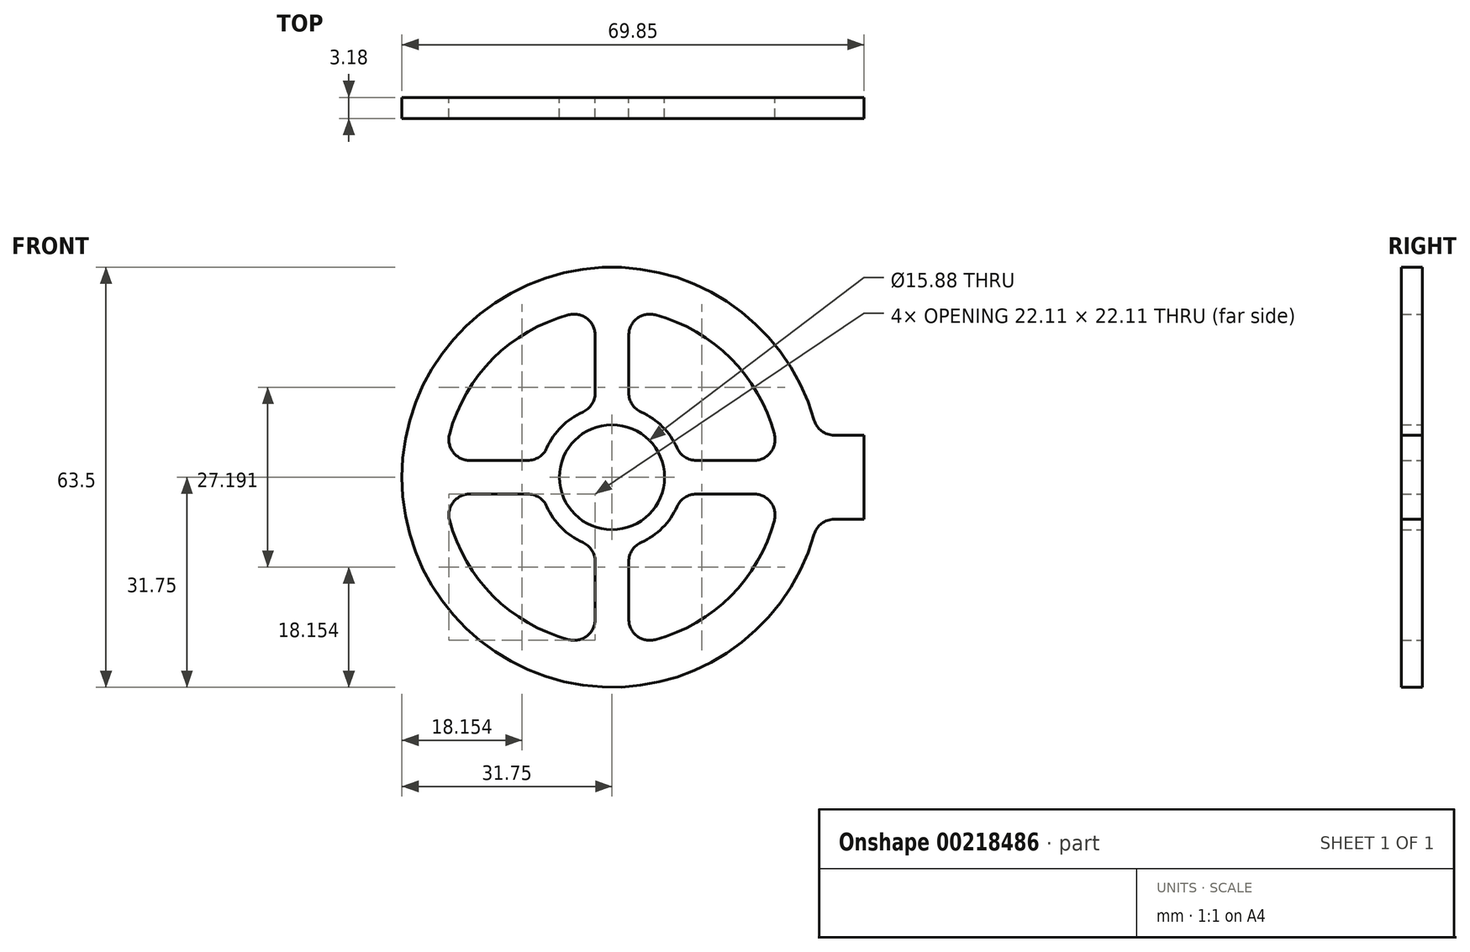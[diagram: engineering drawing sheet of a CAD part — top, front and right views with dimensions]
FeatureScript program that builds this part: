
annotation { "Feature Type Name" : "Feature", "Feature Type Description" : "" }
export const myFeature = defineFeature(function(context is Context, id is Id, definition is map)
    precondition{}
    {
        {
            var Q0;
            Q0=qCreatedBy(makeId("Front.planeOp"),FACE);
            var sketch = newSketch(context, id + "F0", { "sketchPlane" : qUnion([Q0])});
            skArc(sketch, "E0", {"start": v(30.55, 8.66) * mm, "mid": v(-31.75, 0) * mm, "end": v(30.55, -8.66) * mm});
            skLineSegment(sketch, "E1", {"start": v(-12.75, 2.54) * mm, "end": v(-21.48, 2.54) * mm});
            skLineSegment(sketch, "E2", {"start": v(-2.54, 12.75) * mm, "end": v(-2.54, 21.48) * mm});
            skLineSegment(sketch, "E3", {"start": v(2.54, 12.75) * mm, "end": v(2.54, 21.48) * mm});
            skLineSegment(sketch, "E4", {"start": v(12.75, 2.54) * mm, "end": v(21.48, 2.54) * mm});
            skLineSegment(sketch, "E5", {"start": v(-12.75, -2.54) * mm, "end": v(-21.48, -2.54) * mm});
            skLineSegment(sketch, "E6", {"start": v(12.75, -2.54) * mm, "end": v(21.48, -2.54) * mm});
            skLineSegment(sketch, "E7", {"start": v(-2.54, -12.75) * mm, "end": v(-2.54, -21.48) * mm});
            skLineSegment(sketch, "E8", {"start": v(2.54, -12.75) * mm, "end": v(2.54, -21.48) * mm});
            skArc(sketch, "E9", {"start": v(-6.53, 24.55) * mm, "mid": v(-17.96, 17.96) * mm, "end": v(-24.55, 6.53) * mm});
            skArc(sketch, "E10.trimOffspring", {"start": v(-24.55, -6.53) * mm, "mid": v(-17.96, -17.96) * mm, "end": v(-6.53, -24.55) * mm});
            skArc(sketch, "E11.trimOffspring", {"start": v(24.55, 6.53) * mm, "mid": v(17.96, 17.96) * mm, "end": v(6.53, 24.55) * mm});
            skArc(sketch, "E12.trimOffspring", {"start": v(6.53, -24.55) * mm, "mid": v(17.96, -17.96) * mm, "end": v(24.55, -6.53) * mm});
            skPoint(sketch, "E13.visualSharp", {"position": v(-2.54, 25.27) * mm});
            skArc(sketch, "E13.filletArc", {"start": v(-2.54, 21.48) * mm, "mid": v(-3.78, 24) * mm, "end": v(-6.53, 24.55) * mm});
            skPoint(sketch, "E14.visualSharp", {"position": v(-2.54, 2.54) * mm});
            skPoint(sketch, "E15.visualSharp", {"position": v(-25.27, 2.54) * mm});
            skArc(sketch, "E15.filletArc", {"start": v(-24.55, 6.53) * mm, "mid": v(-24, 3.78) * mm, "end": v(-21.48, 2.54) * mm});
            skPoint(sketch, "E16.visualSharp", {"position": v(-25.27, -2.54) * mm});
            skArc(sketch, "E16.filletArc", {"start": v(-21.48, -2.54) * mm, "mid": v(-24, -3.78) * mm, "end": v(-24.55, -6.53) * mm});
            skPoint(sketch, "E17.visualSharp", {"position": v(-2.54, -2.54) * mm});
            skPoint(sketch, "E18.visualSharp", {"position": v(-2.54, -25.27) * mm});
            skArc(sketch, "E18.filletArc", {"start": v(-6.53, -24.55) * mm, "mid": v(-3.78, -24) * mm, "end": v(-2.54, -21.48) * mm});
            skPoint(sketch, "E19.visualSharp", {"position": v(2.54, -25.27) * mm});
            skArc(sketch, "E19.filletArc", {"start": v(2.54, -21.48) * mm, "mid": v(3.78, -24) * mm, "end": v(6.53, -24.55) * mm});
            skPoint(sketch, "E20.visualSharp", {"position": v(25.27, -2.54) * mm});
            skArc(sketch, "E20.filletArc", {"start": v(24.55, -6.53) * mm, "mid": v(24, -3.78) * mm, "end": v(21.48, -2.54) * mm});
            skPoint(sketch, "E21.visualSharp", {"position": v(2.54, -2.54) * mm});
            skPoint(sketch, "E22.visualSharp", {"position": v(2.54, 2.54) * mm});
            skPoint(sketch, "E23.visualSharp", {"position": v(25.27, 2.54) * mm});
            skArc(sketch, "E23.filletArc", {"start": v(21.48, 2.54) * mm, "mid": v(24, 3.78) * mm, "end": v(24.55, 6.53) * mm});
            skPoint(sketch, "E24.visualSharp", {"position": v(2.54, 25.27) * mm});
            skArc(sketch, "E24.filletArc", {"start": v(6.53, 24.55) * mm, "mid": v(3.78, 24) * mm, "end": v(2.54, 21.48) * mm});
            skArc(sketch, "E25", {"start": v(9.85, 4.42) * mm, "mid": v(7.63, 7.63) * mm, "end": v(4.42, 9.85) * mm});
            skArc(sketch, "E26.trimOffspring", {"start": v(-4.42, 9.85) * mm, "mid": v(-7.63, 7.63) * mm, "end": v(-9.85, 4.42) * mm});
            skArc(sketch, "E27.trimOffspring", {"start": v(-9.85, -4.42) * mm, "mid": v(-7.63, -7.63) * mm, "end": v(-4.42, -9.85) * mm});
            skArc(sketch, "E28.trimOffspring", {"start": v(4.42, -9.85) * mm, "mid": v(7.63, -7.63) * mm, "end": v(9.85, -4.42) * mm});
            skCircle(sketch, "E29", {"center": v(0, 0) * mm, "radius": 7.94 * mm});
            skPoint(sketch, "E30.visualSharp", {"position": v(-2.54, 10.5) * mm});
            skArc(sketch, "E30.filletArc", {"start": v(-4.42, 9.85) * mm, "mid": v(-3.05, 11.02) * mm, "end": v(-2.54, 12.75) * mm});
            skPoint(sketch, "E31.visualSharp", {"position": v(-10.5, 2.54) * mm});
            skArc(sketch, "E31.filletArc", {"start": v(-12.75, 2.54) * mm, "mid": v(-11.02, 3.05) * mm, "end": v(-9.85, 4.42) * mm});
            skPoint(sketch, "E32.visualSharp", {"position": v(-10.5, -2.54) * mm});
            skArc(sketch, "E32.filletArc", {"start": v(-9.85, -4.42) * mm, "mid": v(-11.02, -3.05) * mm, "end": v(-12.75, -2.54) * mm});
            skPoint(sketch, "E33.visualSharp", {"position": v(-2.54, -10.5) * mm});
            skArc(sketch, "E33.filletArc", {"start": v(-2.54, -12.75) * mm, "mid": v(-3.05, -11.02) * mm, "end": v(-4.42, -9.85) * mm});
            skPoint(sketch, "E34.visualSharp", {"position": v(2.54, -10.5) * mm});
            skArc(sketch, "E34.filletArc", {"start": v(4.42, -9.85) * mm, "mid": v(3.05, -11.02) * mm, "end": v(2.54, -12.75) * mm});
            skPoint(sketch, "E35.visualSharp", {"position": v(10.5, -2.54) * mm});
            skArc(sketch, "E35.filletArc", {"start": v(12.75, -2.54) * mm, "mid": v(11.02, -3.05) * mm, "end": v(9.85, -4.42) * mm});
            skPoint(sketch, "E36.visualSharp", {"position": v(10.5, 2.54) * mm});
            skArc(sketch, "E36.filletArc", {"start": v(9.85, 4.42) * mm, "mid": v(11.02, 3.05) * mm, "end": v(12.75, 2.54) * mm});
            skPoint(sketch, "E37.visualSharp", {"position": v(2.54, 10.5) * mm});
            skArc(sketch, "E37.filletArc", {"start": v(2.54, 12.75) * mm, "mid": v(3.05, 11.02) * mm, "end": v(4.42, 9.85) * mm});
            skLineSegment(sketch, "E38", {"start": v(33.6, 6.35) * mm, "end": v(38.1, 6.35) * mm});
            skLineSegment(sketch, "E39", {"start": v(38.1, 6.35) * mm, "end": v(38.1, -6.35) * mm});
            skLineSegment(sketch, "E40", {"start": v(38.1, -6.35) * mm, "end": v(33.6, -6.35) * mm});
            skPoint(sketch, "E41.visualSharp", {"position": v(31.1, 6.35) * mm});
            skArc(sketch, "E41.filletArc", {"start": v(30.55, 8.66) * mm, "mid": v(31.69, 7) * mm, "end": v(33.6, 6.35) * mm});
            skPoint(sketch, "E42.visualSharp", {"position": v(31.1, -6.35) * mm});
            skArc(sketch, "E42.filletArc", {"start": v(33.6, -6.35) * mm, "mid": v(31.69, -7) * mm, "end": v(30.55, -8.66) * mm});
            skSolve(sketch);
        }
        {
            var Q0;
            Q0 = qSketchRegion(id + "F0", true);
            extrude(context, id + "F1", {"entities" : qUnion([Q0]), "depth" : 3.17 * mm});
        }
    });
